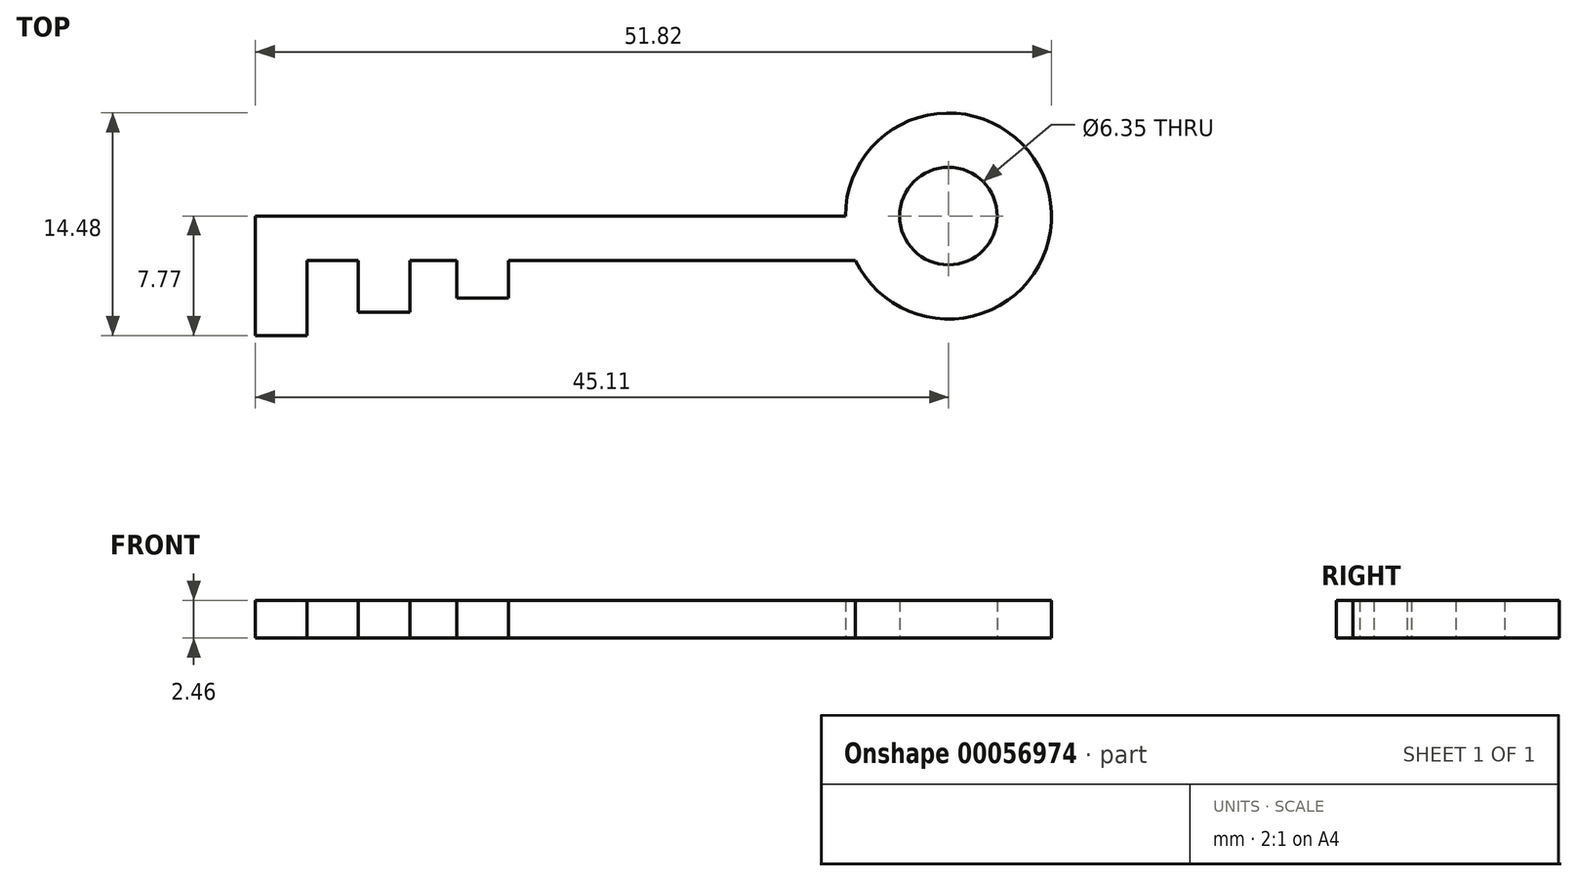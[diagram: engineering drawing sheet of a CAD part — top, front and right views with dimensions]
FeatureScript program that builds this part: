
annotation { "Feature Type Name" : "Feature", "Feature Type Description" : "" }
export const myFeature = defineFeature(function(context is Context, id is Id, definition is map)
    precondition{}
    {
        {
            var Q0;
            Q0=qCreatedBy(makeId("Top.planeOp"),FACE);
            var sketch = newSketch(context, id + "F0", { "sketchPlane" : qUnion([Q0])});
            skCircle(sketch, "E0", {"center": v(0, 0) * mm, "radius": 6.7 * mm});
            skLineSegment(sketch, "E1", {"start": v(-6.7, 0) * mm, "end": v(-45.11, 0) * mm});
            skLineSegment(sketch, "E2", {"start": v(-45.11, 0) * mm, "end": v(-45.11, -7.77) * mm});
            skLineSegment(sketch, "E3", {"start": v(-45.11, -7.77) * mm, "end": v(-41.76, -7.77) * mm});
            skLineSegment(sketch, "E4", {"start": v(-41.76, -7.77) * mm, "end": v(-41.76, -2.9) * mm});
            skLineSegment(sketch, "E5", {"start": v(-41.76, -2.9) * mm, "end": v(-38.4, -2.9) * mm});
            skLineSegment(sketch, "E6", {"start": v(-38.4, -2.9) * mm, "end": v(-38.4, -6.25) * mm});
            skLineSegment(sketch, "E7", {"start": v(-38.4, -6.25) * mm, "end": v(-35.05, -6.25) * mm});
            skLineSegment(sketch, "E8", {"start": v(-35.05, -6.25) * mm, "end": v(-35.05, -2.9) * mm});
            skLineSegment(sketch, "E9", {"start": v(-35.05, -2.9) * mm, "end": v(-32, -2.9) * mm});
            skLineSegment(sketch, "E10", {"start": v(-32, -2.9) * mm, "end": v(-32, -5.33) * mm});
            skLineSegment(sketch, "E11", {"start": v(-32, -5.33) * mm, "end": v(-28.65, -5.33) * mm});
            skLineSegment(sketch, "E12", {"start": v(-28.65, -5.33) * mm, "end": v(-28.65, -2.9) * mm});
            skLineSegment(sketch, "E13", {"start": v(-28.65, -2.9) * mm, "end": v(-6.05, -2.9) * mm});
            skSolve(sketch);
        }
        {
            var Q0;
            Q0 = qSketchRegion(id + "F0", true);
            extrude(context, id + "F1", {"entities" : qUnion([Q0]), "depth" : 2.46 * mm});
        }
        {
            var Q0;
            Q0=sQuery(id+"F0.wireOp",VERTEX,"E0.center");
            var Q1;
            Q1=makeQuery(id+"F1.opExtrude","SWEPT_BODY",BODY,{"disambiguationData":[OSD([sQuery(id+"F0.wireOp",EDGE,"E0"),sQuery(id+"F0.wireOp",EDGE,"E1"),sQuery(id+"F0.wireOp",EDGE,"E2"),sQuery(id+"F0.wireOp",EDGE,"E3"),sQuery(id+"F0.wireOp",EDGE,"E4"),sQuery(id+"F0.wireOp",EDGE,"E5"),sQuery(id+"F0.wireOp",EDGE,"E6"),sQuery(id+"F0.wireOp",EDGE,"E7"),sQuery(id+"F0.wireOp",EDGE,"E8"),sQuery(id+"F0.wireOp",EDGE,"E9"),sQuery(id+"F0.wireOp",EDGE,"E10"),sQuery(id+"F0.wireOp",EDGE,"E11"),sQuery(id+"F0.wireOp",EDGE,"E12"),sQuery(id+"F0.wireOp",EDGE,"E13")])]});
            hole(context, id + "F2", {"style" : HoleStyle.SIMPLE, "holeDiameter" : 6.35 * mm, "endStyle" : HoleEndStyle.THROUGH, "oppositeDirection" : true, "locations" : qUnion([Q0]), "scope" : qUnion([Q1])});
        }
    });
